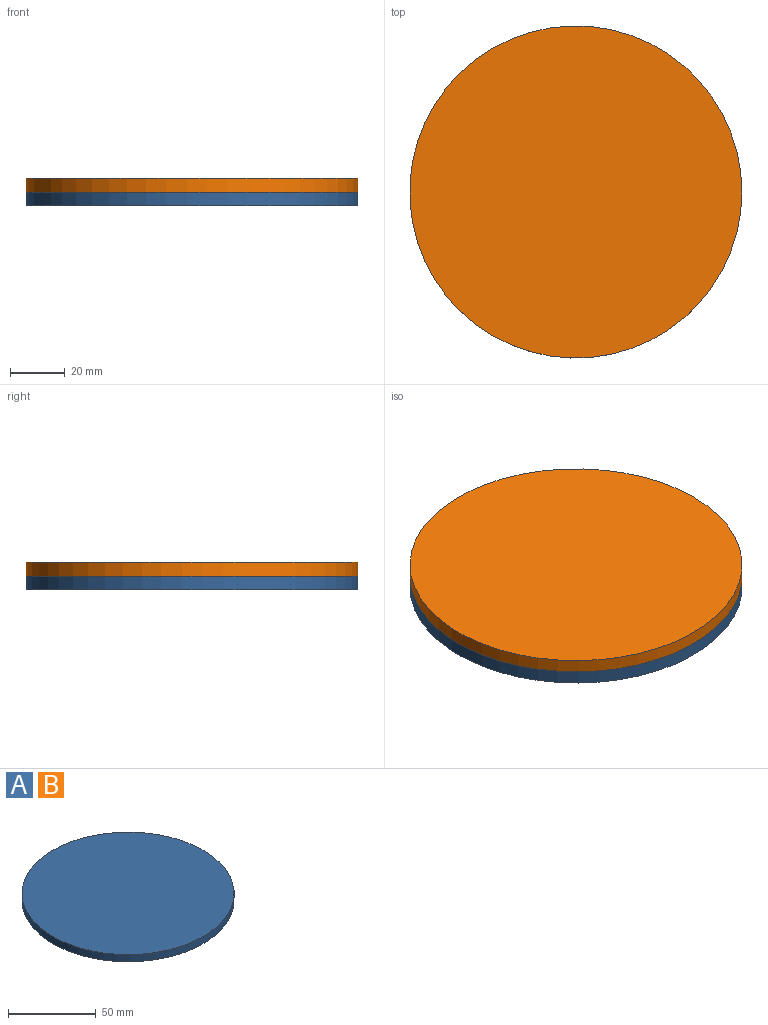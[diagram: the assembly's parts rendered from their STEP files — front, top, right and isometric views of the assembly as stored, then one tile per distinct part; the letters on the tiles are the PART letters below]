
ASSEMBLY  parts=2 mates=1
PART A: 3 faces, bbox 121.1x121.1x5 mm
  f0: cylinder r=60.56mm len=121.12mm, axis (0,0,-1), area 1902.6mm2, adj f1,f2
  f1: plane 121.12x121.12mm, normal (0,0,1), area 11522.6mm2, adj f0
  f2: plane 121.12x121.12mm, normal (0,0,-1), area 11522.6mm2, adj f0
PART B: same geometry as A
PLACE A t=(-0.21,-0.03,-2.36)mm
PLACE B t=(-0.21,-0.03,2.64)mm
MATE fastened B.f0 <-> A.f0  axis (0,0,-1) through (-0.21,-0.03,2.64)mm
